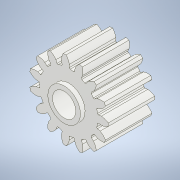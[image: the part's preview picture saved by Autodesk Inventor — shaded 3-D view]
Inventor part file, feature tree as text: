
AUTODESK INVENTOR PART (.ipt)
format: ipt  version: 2022 (Build 260153000, 153)  size: 410,112 bytes
history: native  units: in
note: dims shown in document units (in); Inventor stores cm internally (conversion verified against a paired STEP export)
features: extrude x2, sketch x2
ambient origin geometry x8: Origin, YZ Plane, XZ Plane, XY Plane, X Axis, Y Axis, Z Axis, Center Point
bodies: Solid1 (feature_tree), Body1 (feature_tree)
feature tree (4):
  extrude  "Extrusion1"  Depth=0.3937in TaperAngle=0.0deg
  extrude  "Extrusion2"  Depth=0.0394in TaperAngle=0.0deg
  sketch  "Sketch1"  dims[d0=0.1969in d1=0.3937in d2=0.0in]
  sketch  "Sketch2"  dims[d3=0.0394in d4=0.0394in d5=0.0in]
